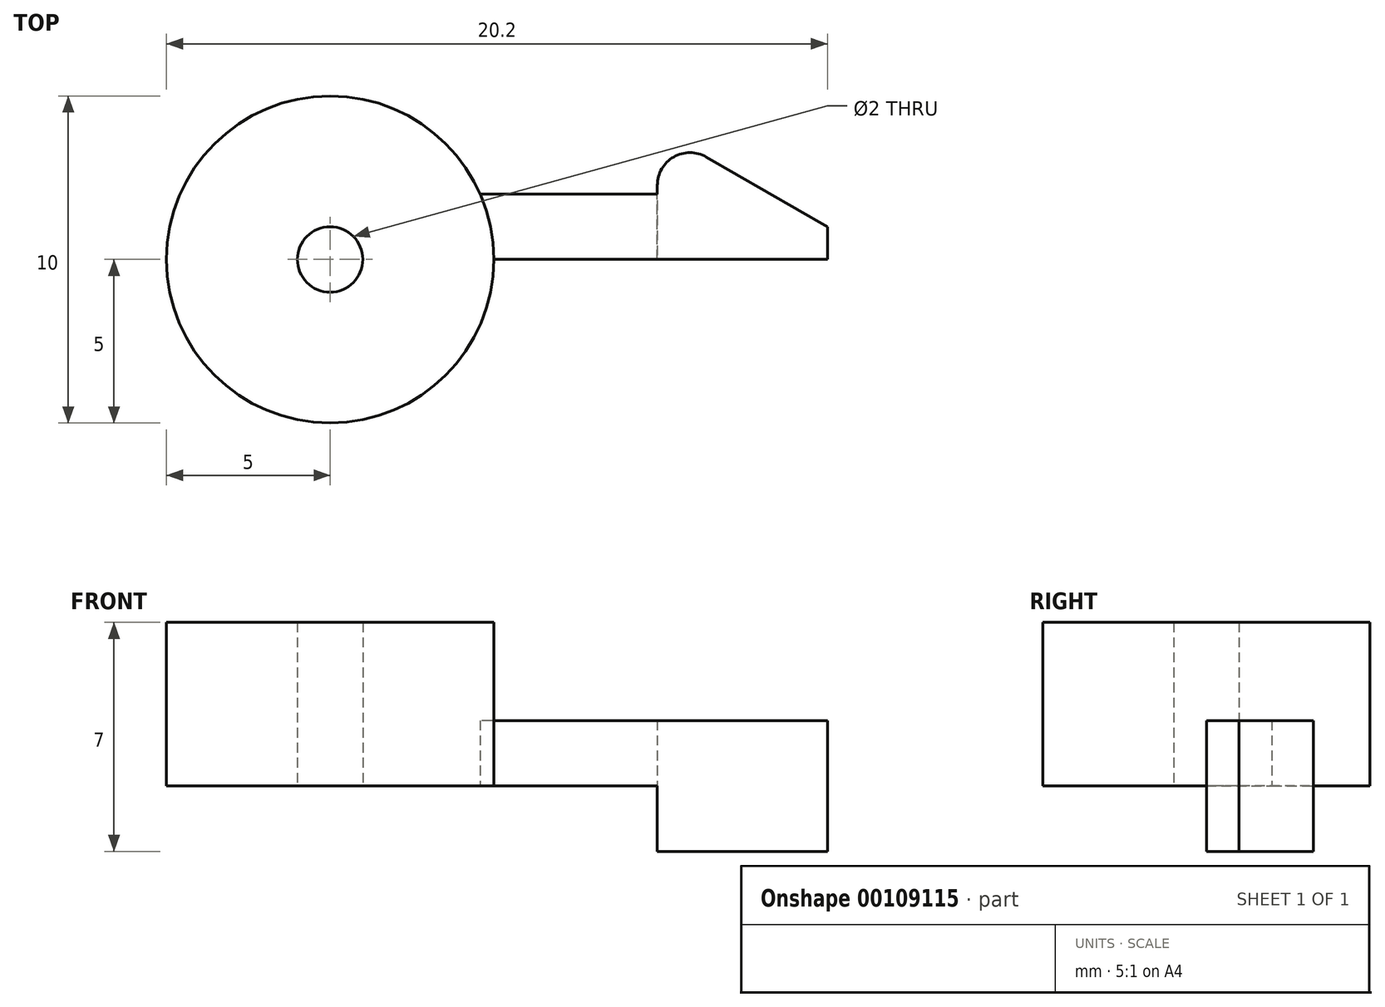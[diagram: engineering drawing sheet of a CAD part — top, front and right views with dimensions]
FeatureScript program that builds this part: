
annotation { "Feature Type Name" : "Feature", "Feature Type Description" : "" }
export const myFeature = defineFeature(function(context is Context, id is Id, definition is map)
    precondition{}
    {
        {
            var Q0;
            Q0=qCreatedBy(makeId("Top.planeOp"),FACE);
            var sketch = newSketch(context, id + "F0", { "sketchPlane" : qUnion([Q0])});
            skCircle(sketch, "E0", {"center": v(0, 0) * mm, "radius": 5 * mm});
            skLineSegment(sketch, "E1", {"start": v(5, 0) * mm, "end": v(10, 0) * mm});
            skLineSegment(sketch, "E2", {"start": v(10, 0) * mm, "end": v(10, 2) * mm});
            skLineSegment(sketch, "E3", {"start": v(10, 2) * mm, "end": v(4.58, 2) * mm});
            skLineSegment(sketch, "E4", {"start": v(10, 0) * mm, "end": v(15.2, 0) * mm});
            skLineSegment(sketch, "E5", {"start": v(15.2, 0) * mm, "end": v(15.2, 1) * mm});
            skLineSegment(sketch, "E6", {"start": v(15.2, 1) * mm, "end": v(10, 4) * mm});
            skLineSegment(sketch, "E7", {"start": v(10, 4) * mm, "end": v(10, 2) * mm});
            skSolve(sketch);
        }
        {
            var Q0;
            {var subQ0=sQuery(id+"F0.wireOp",EDGE,"E0");var subQ1=makeQuery(id+"F0.imprint","INTERSECT",VERTEX,{"derivedFrom":[subQ0,sQuery(id+"F0.wireOp",EDGE,"E1")]});Q0=makeQuery(id+"F0.imprint","IMPRINT",FACE,{"disambiguationData":[TD([[makeQuery(id+"F0.imprint","IMPRINT",EDGE,{"disambiguationData":[TD([[subQ1,-1.0]])],"derivedFrom":subQ0}),1.0]])]});}
            extrude(context, id + "F1", {"entities" : qUnion([Q0]), "depth" : 5 * mm});
        }
        {
            var Q0;
            {var subQ0=sQuery(id+"F0.wireOp",EDGE,"E1");Q0=makeQuery(id+"F0.imprint","IMPRINT",FACE,{"disambiguationData":[TD([[makeQuery(id+"F0.imprint","IMPRINT",EDGE,{"derivedFrom":subQ0}),1.0]])]});}
            extrude(context, id + "F2", {"entities" : qUnion([Q0]), "operationType" : NewBodyOperationType.ADD, "depth" : 2 * mm});
        }
        {
            var Q0;
            Q0=makeQuery(id+"F0.imprint","IMPRINT",FACE,{"disambiguationData":[TD([[makeQuery(id+"F0.imprint","IMPRINT",EDGE,{"derivedFrom":sQuery(id+"F0.wireOp",EDGE,"E2")}),-1.0]])]});
            extrude(context, id + "F3", {"entities" : qUnion([Q0]), "operationType" : NewBodyOperationType.ADD, "endBound" : BoundingType.SYMMETRIC, "depth" : 4 * mm});
        }
        {
            var Q0;
            Q0=makeQuery(id+"F3.opExtrude","SWEPT_EDGE",EDGE,{"disambiguationData":[OSD([sQuery(id+"F0.wireOp",EDGE,"E6"),sQuery(id+"F0.wireOp",EDGE,"E7")])]});
            fillet(context, id + "F4", {"entities" : qUnion([Q0]), "radius" : mm, "tangentPropagation" : true, "allowEdgeOverflow" : false});
        }
        {
            var Q0;
            Q0=sQuery(id+"F0.wireOp",VERTEX,"E0.center");
            var Q1;
            Q1=makeQuery(id+"F1.opExtrude","SWEPT_BODY",BODY,{"disambiguationData":[OSD([sQuery(id+"F0.wireOp",EDGE,"E0")])]});
            hole(context, id + "F5", {"style" : HoleStyle.SIMPLE, "endStyle" : HoleEndStyle.THROUGH, "oppositeDirection" : true, "holeDiameter" : 2 * mm, "locations" : qUnion([Q0]), "scope" : qUnion([Q1]), "isTappedThrough" : true});
        }
    });
